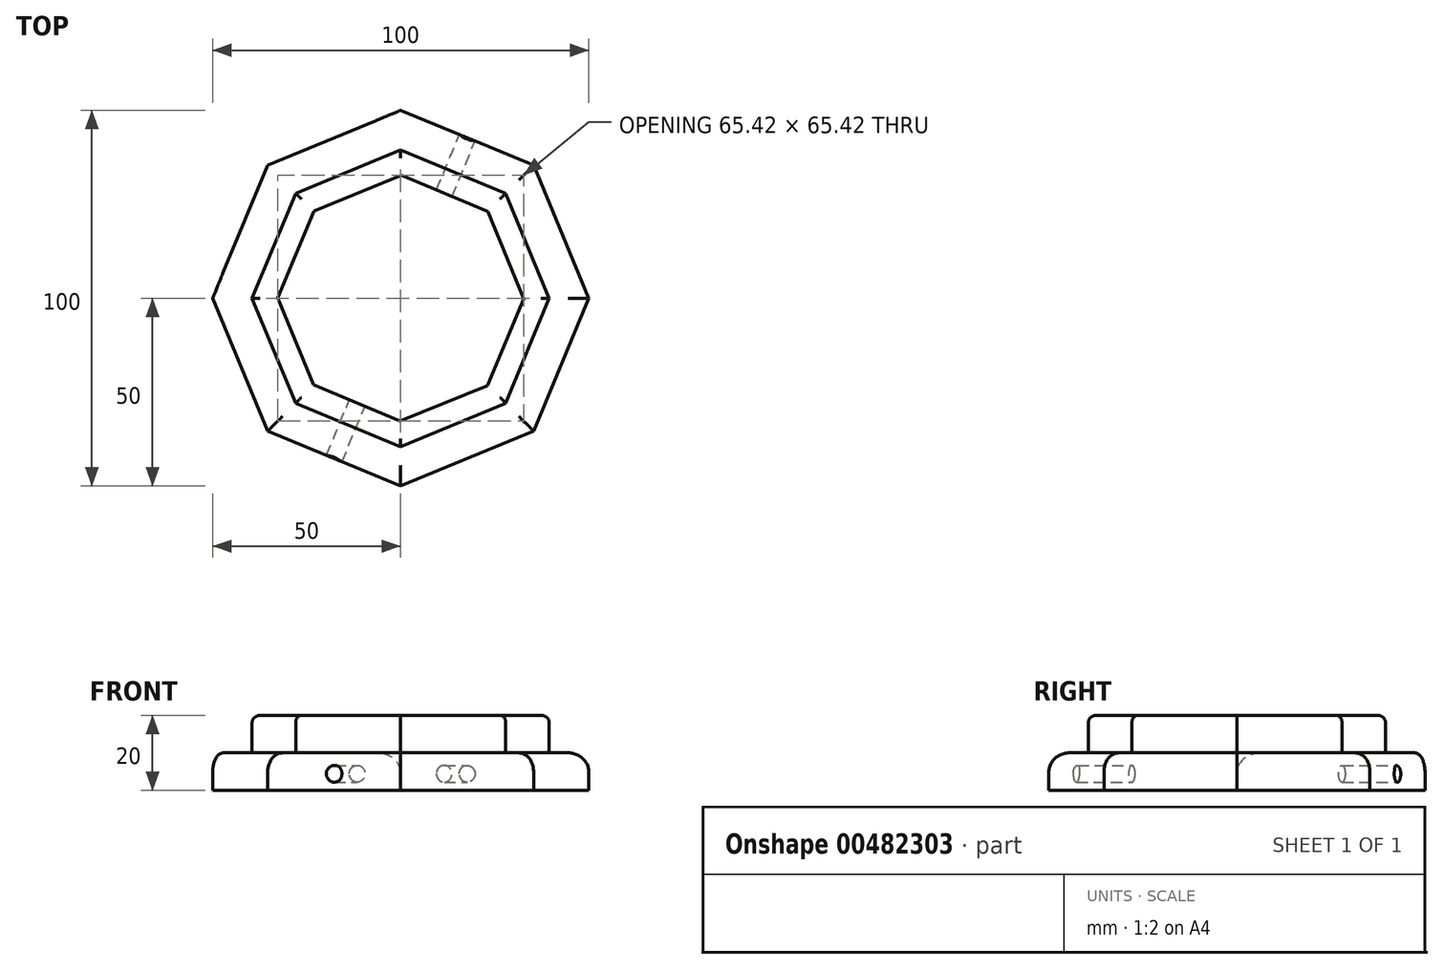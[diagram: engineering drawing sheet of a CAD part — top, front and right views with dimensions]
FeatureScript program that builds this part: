
annotation { "Feature Type Name" : "Feature", "Feature Type Description" : "" }
export const myFeature = defineFeature(function(context is Context, id is Id, definition is map)
    precondition{}
    {
        {
            var Q0;
            Q0=qCreatedBy(makeId("Top.planeOp"),FACE);
            var sketch = newSketch(context, id + "F0", { "sketchPlane" : qUnion([Q0])});
            skCircle(sketch, "E0.cCircle", {"center": v(0, 0) * mm, "radius": 46.2 * mm, "construction": true});
            skLineSegment(sketch, "E0.0", {"start": v(35.36, 35.36) * mm, "end": v(50, 0) * mm});
            skLineSegment(sketch, "E0.1", {"start": v(50, 0) * mm, "end": v(35.36, -35.36) * mm});
            skLineSegment(sketch, "E0.2", {"start": v(35.36, -35.36) * mm, "end": v(0, -50) * mm});
            skLineSegment(sketch, "E0.3", {"start": v(0, -50) * mm, "end": v(-35.36, -35.36) * mm});
            skLineSegment(sketch, "E0.4", {"start": v(-35.36, -35.36) * mm, "end": v(-50, 0) * mm});
            skLineSegment(sketch, "E0.5", {"start": v(-50, 0) * mm, "end": v(-35.36, 35.36) * mm});
            skLineSegment(sketch, "E0.6", {"start": v(-35.36, 35.36) * mm, "end": v(0, 50) * mm});
            skLineSegment(sketch, "E0.7", {"start": v(0, 50) * mm, "end": v(35.36, 35.36) * mm});
            skPoint(sketch, "E0.0.midPoint", {"position": v(42.68, 17.68) * mm});
            skSolve(sketch);
        }
        {
            var Q0;
            Q0=makeQuery(id+"F0.imprint","IMPRINT",FACE,{"disambiguationData":[TD([[makeQuery(id+"F0.imprint","IMPRINT",EDGE,{"derivedFrom":sQuery(id+"F0.wireOp",EDGE,"E0.0")}),-1.0]])]});
            extrude(context, id + "F1", {"entities" : qUnion([Q0]), "oppositeDirection" : true, "depth" : 10 * mm});
        }
        {
            var Q0;
            Q0=makeQuery(id+"F1.opExtrude","CAP_FACE",FACE,{"disambiguationData":[OSD([sQuery(id+"F0.wireOp",EDGE,"E0.0"),sQuery(id+"F0.wireOp",EDGE,"E0.1"),sQuery(id+"F0.wireOp",EDGE,"E0.2"),sQuery(id+"F0.wireOp",EDGE,"E0.3"),sQuery(id+"F0.wireOp",EDGE,"E0.4"),sQuery(id+"F0.wireOp",EDGE,"E0.5"),sQuery(id+"F0.wireOp",EDGE,"E0.6"),sQuery(id+"F0.wireOp",EDGE,"E0.7")])],"isStart":true});
            var sketch = newSketch(context, id + "F2", { "sketchPlane" : qUnion([Q0])});
            skCircle(sketch, "E1.cCircle", {"center": v(0, 0) * mm, "radius": 36.5 * mm, "construction": true});
            skLineSegment(sketch, "E1.0", {"start": v(0, -39.5) * mm, "end": v(-27.93, -27.93) * mm});
            skLineSegment(sketch, "E1.1", {"start": v(-27.93, -27.93) * mm, "end": v(-39.5, 0) * mm});
            skLineSegment(sketch, "E1.2", {"start": v(-39.5, 0) * mm, "end": v(-27.93, 27.93) * mm});
            skLineSegment(sketch, "E1.3", {"start": v(-27.93, 27.93) * mm, "end": v(0, 39.5) * mm});
            skLineSegment(sketch, "E1.4", {"start": v(0, 39.5) * mm, "end": v(27.93, 27.93) * mm});
            skLineSegment(sketch, "E1.5", {"start": v(27.93, 27.93) * mm, "end": v(39.5, 0) * mm});
            skLineSegment(sketch, "E1.6", {"start": v(39.5, 0) * mm, "end": v(27.93, -27.93) * mm});
            skLineSegment(sketch, "E1.7", {"start": v(27.93, -27.93) * mm, "end": v(0, -39.5) * mm});
            skPoint(sketch, "E1.0.midPoint", {"position": v(-13.97, -33.72) * mm});
            skSolve(sketch);
        }
        {
            var Q0;
            Q0=makeQuery(id+"F2.imprint","IMPRINT",FACE,{"disambiguationData":[TD([[makeQuery(id+"F2.imprint","IMPRINT",EDGE,{"derivedFrom":sQuery(id+"F2.wireOp",EDGE,"E1.0")}),-1.0]])]});
            extrude(context, id + "F3", {"entities" : qUnion([Q0]), "operationType" : NewBodyOperationType.ADD, "depth" : 10 * mm});
        }
        {
            var Q0;
            Q0=makeQuery(id+"F3.opExtrude","CAP_FACE",FACE,{"disambiguationData":[OSD([sQuery(id+"F2.wireOp",EDGE,"E1.0"),sQuery(id+"F2.wireOp",EDGE,"E1.1"),sQuery(id+"F2.wireOp",EDGE,"E1.2"),sQuery(id+"F2.wireOp",EDGE,"E1.3"),sQuery(id+"F2.wireOp",EDGE,"E1.4"),sQuery(id+"F2.wireOp",EDGE,"E1.5"),sQuery(id+"F2.wireOp",EDGE,"E1.6"),sQuery(id+"F2.wireOp",EDGE,"E1.7")])],"isStart":false});
            var sketch = newSketch(context, id + "F4", { "sketchPlane" : qUnion([Q0])});
            skCircle(sketch, "E2.cCircle", {"center": v(0, 0) * mm, "radius": 30.22 * mm, "construction": true});
            skLineSegment(sketch, "E2.0", {"start": v(-23.23, -23.03) * mm, "end": v(-32.71, 0.14) * mm});
            skLineSegment(sketch, "E2.1", {"start": v(-32.71, 0.14) * mm, "end": v(-23.03, 23.23) * mm});
            skLineSegment(sketch, "E2.2", {"start": v(-23.03, 23.23) * mm, "end": v(0.14, 32.71) * mm});
            skLineSegment(sketch, "E2.3", {"start": v(0.14, 32.71) * mm, "end": v(23.23, 23.03) * mm});
            skLineSegment(sketch, "E2.4", {"start": v(23.23, 23.03) * mm, "end": v(32.71, -0.14) * mm});
            skLineSegment(sketch, "E2.5", {"start": v(32.71, -0.14) * mm, "end": v(23.03, -23.23) * mm});
            skLineSegment(sketch, "E2.6", {"start": v(23.03, -23.23) * mm, "end": v(-0.14, -32.71) * mm});
            skLineSegment(sketch, "E2.7", {"start": v(-0.14, -32.71) * mm, "end": v(-23.23, -23.03) * mm});
            skPoint(sketch, "E2.0.midPoint", {"position": v(-27.97, -11.44) * mm});
            skSolve(sketch);
        }
        {
            var Q0;
            Q0=makeQuery(id+"F4.imprint","IMPRINT",FACE,{"disambiguationData":[TD([[makeQuery(id+"F4.imprint","IMPRINT",EDGE,{"derivedFrom":sQuery(id+"F4.wireOp",EDGE,"E2.0")}),-1.0]])]});
            extrude(context, id + "F5", {"entities" : qUnion([Q0]), "operationType" : NewBodyOperationType.REMOVE, "oppositeDirection" : true, "depth" : 23.65 * mm});
        }
        {
            var Q0;
            Q0=makeQuery(id+"F1.opExtrude","SWEPT_FACE",FACE,{"disambiguationData":[OSD([sQuery(id+"F0.wireOp",EDGE,"E0.7")])]});
            var sketch = newSketch(context, id + "F6", { "sketchPlane" : qUnion([Q0])});
            skCircle(sketch, "E3", {"center": v(0, -5.57) * mm, "radius": 6.5 * mm});
            skPoint(sketch, "E3.centerSnap0", {"position": v(0, -10) * mm});
            skCircle(sketch, "E4", {"center": v(0, -5.57) * mm, "radius": 2.25 * mm});
            skSolve(sketch);
        }
        {
            var Q0;
            Q0=makeQuery(id+"F6.imprint","IMPRINT",FACE,{"disambiguationData":[TD([[makeQuery(id+"F6.imprint","IMPRINT",EDGE,{"derivedFrom":sQuery(id+"F6.wireOp",EDGE,"E4")}),1.0]])]});
            extrude(context, id + "F7", {"entities" : qUnion([Q0]), "operationType" : NewBodyOperationType.REMOVE, "oppositeDirection" : true, "depth" : 107.7 * mm});
        }
        {
            var Q0;
            Q0=makeQuery(id+"F3.opExtrude","CAP_EDGE",EDGE,{"disambiguationData":[OSD([sQuery(id+"F2.wireOp",EDGE,"E1.5")])],"isStart":false});
            var Q1;
            Q1=makeQuery(id+"F3.opExtrude","CAP_EDGE",EDGE,{"disambiguationData":[OSD([sQuery(id+"F2.wireOp",EDGE,"E1.6")])],"isStart":false});
            var Q2;
            Q2=makeQuery(id+"F3.opExtrude","CAP_EDGE",EDGE,{"disambiguationData":[OSD([sQuery(id+"F2.wireOp",EDGE,"E1.7")])],"isStart":false});
            var Q3;
            Q3=makeQuery(id+"F3.opExtrude","CAP_EDGE",EDGE,{"disambiguationData":[OSD([sQuery(id+"F2.wireOp",EDGE,"E1.0")])],"isStart":false});
            var Q4;
            Q4=makeQuery(id+"F3.opExtrude","CAP_EDGE",EDGE,{"disambiguationData":[OSD([sQuery(id+"F2.wireOp",EDGE,"E1.1")])],"isStart":false});
            var Q5;
            Q5=makeQuery(id+"F3.opExtrude","CAP_EDGE",EDGE,{"disambiguationData":[OSD([sQuery(id+"F2.wireOp",EDGE,"E1.2")])],"isStart":false});
            var Q6;
            Q6=makeQuery(id+"F3.opExtrude","CAP_EDGE",EDGE,{"disambiguationData":[OSD([sQuery(id+"F2.wireOp",EDGE,"E1.3")])],"isStart":false});
            var Q7;
            Q7=makeQuery(id+"F3.opExtrude","CAP_EDGE",EDGE,{"disambiguationData":[OSD([sQuery(id+"F2.wireOp",EDGE,"E1.4")])],"isStart":false});
            fillet(context, id + "F8", {"entities" : qUnion([Q0, Q1, Q2, Q3, Q4, Q5, Q6, Q7]), "radius" : 2 * mm, "tangentPropagation" : true, "allowEdgeOverflow" : false});
        }
        {
            var Q0;
            Q0=makeQuery(id+"F1.opExtrude","CAP_EDGE",EDGE,{"disambiguationData":[OSD([sQuery(id+"F0.wireOp",EDGE,"E0.1")])],"isStart":true});
            var Q1;
            Q1=makeQuery(id+"F1.opExtrude","CAP_EDGE",EDGE,{"disambiguationData":[OSD([sQuery(id+"F0.wireOp",EDGE,"E0.2")])],"isStart":true});
            var Q2;
            Q2=makeQuery(id+"F1.opExtrude","CAP_EDGE",EDGE,{"disambiguationData":[OSD([sQuery(id+"F0.wireOp",EDGE,"E0.3")])],"isStart":true});
            var Q3;
            Q3=makeQuery(id+"F1.opExtrude","CAP_EDGE",EDGE,{"disambiguationData":[OSD([sQuery(id+"F0.wireOp",EDGE,"E0.0")])],"isStart":true});
            var Q4;
            Q4=makeQuery(id+"F1.opExtrude","CAP_EDGE",EDGE,{"disambiguationData":[OSD([sQuery(id+"F0.wireOp",EDGE,"E0.4")])],"isStart":true});
            var Q5;
            Q5=makeQuery(id+"F1.opExtrude","CAP_EDGE",EDGE,{"disambiguationData":[OSD([sQuery(id+"F0.wireOp",EDGE,"E0.7")])],"isStart":true});
            fillet(context, id + "F9", {"entities" : qUnion([Q0, Q1, Q2, Q3, Q4, Q5]), "radius" : 5.08 * mm, "tangentPropagation" : true, "allowEdgeOverflow" : false});
        }
    });
